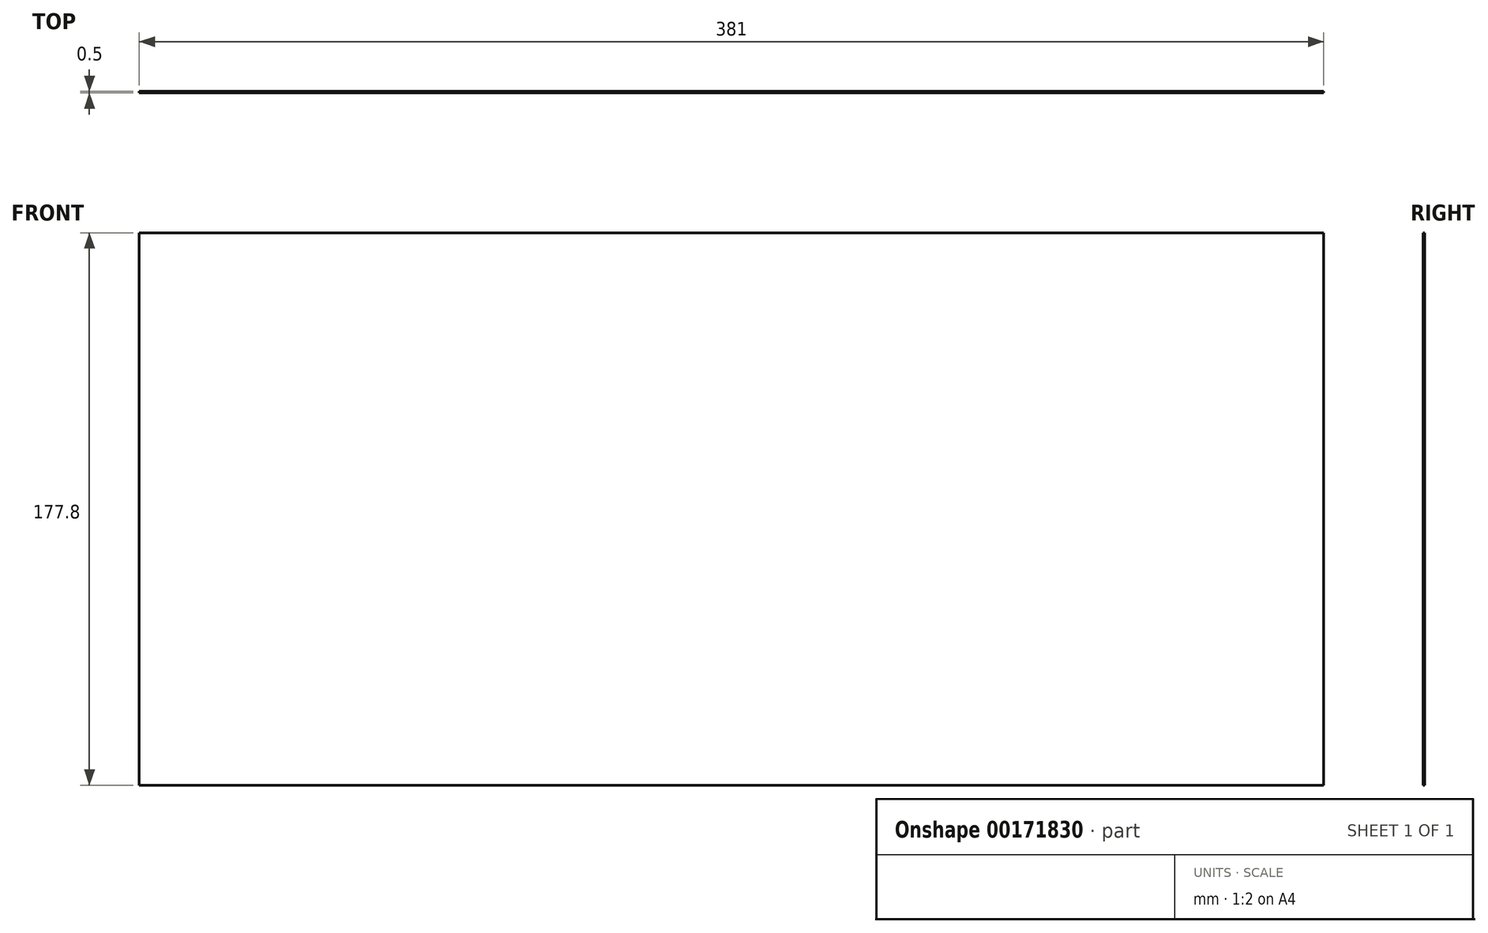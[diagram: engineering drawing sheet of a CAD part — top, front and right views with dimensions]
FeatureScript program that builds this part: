
annotation { "Feature Type Name" : "Feature", "Feature Type Description" : "" }
export const myFeature = defineFeature(function(context is Context, id is Id, definition is map)
    precondition{}
    {
        {
            var Q0;
            Q0=qCreatedBy(makeId("Front.planeOp"),FACE);
            var sketch = newSketch(context, id + "F0", { "sketchPlane" : qUnion([Q0])});
            skLineSegment(sketch, "E0.bottom", {"start": v(0, 0) * mm, "end": v(381, 0) * mm});
            skLineSegment(sketch, "E0.top", {"start": v(0, -177.8) * mm, "end": v(381, -177.8) * mm});
            skLineSegment(sketch, "E0.left", {"start": v(0, 0) * mm, "end": v(0, -177.8) * mm});
            skLineSegment(sketch, "E0.right", {"start": v(381, 0) * mm, "end": v(381, -177.8) * mm});
            skSolve(sketch);
        }
        {
            assignVariable(context, id + "F1", {"name" : "board_thickness", "anyValue" : .5});
        }
        {
            var Q0;
            Q0=makeQuery(id+"F0.imprint","IMPRINT",FACE,{"disambiguationData":[TD([[makeQuery(id+"F0.imprint","IMPRINT",EDGE,{"derivedFrom":sQuery(id+"F0.wireOp",EDGE,"E0.bottom")}),-1.0]])]});
            extrude(context, id + "F2", {"entities" : qUnion([Q0]), "depth" : (getVariable(context, 'board_thickness')) * mm});
        }
    });
